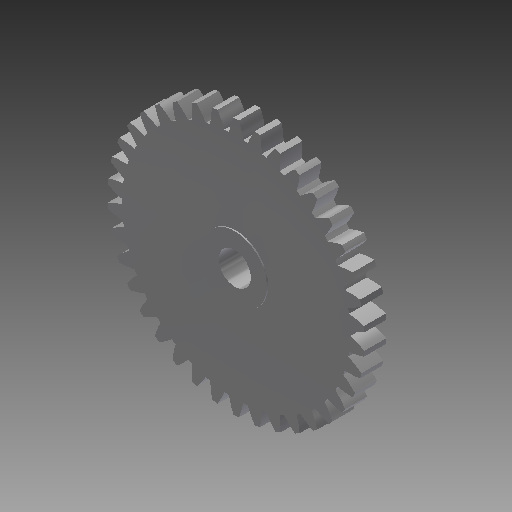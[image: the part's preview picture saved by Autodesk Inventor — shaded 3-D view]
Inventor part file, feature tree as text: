
AUTODESK INVENTOR PART (.ipt)
format: ipt  version: 2017 (Build 210142000, 142)  size: 308,736 bytes
history: native  units: mm (DEFAULTED — no unit token found)
features: sketch x5, extrude x4, plane x3, other x3
ambient origin geometry x8: Origin, YZ Plane, XZ Plane, XY Plane, X Axis, Y Axis, Z Axis, Center Point
bodies: Solid1 (feature_tree)
feature tree (15):
  extrude  "Extrusion1"  Depth=1.7mm TaperAngle=0.0deg
  plane  "Work Plane2"
  plane  "Work Plane8"
  plane  "Work Plane9"
  other  "Spur Gear"
  extrude  "Extrusion2"  Depth=10.0mm TaperAngle=0.0deg
  extrude  "Extrusion3"  Depth=0.826735mm TaperAngle=0.0deg
  extrude  "Extrusion4"  TaperAngle=0.0deg  [1 undecoded]
  sketch  "Sketch1"  dims[d0=20.0mm d1=1.7mm d2=0.0mm]
  sketch  "Sketch2"  dims[d3=19.0mm d4=10.0mm d5=0.0mm]
  other  "Srf1"
  sketch  "Sketch3"  dims[d16=14.5mm d17=0.0mm d34=0.826735mm]
  sketch  "Sketch4"  dims[d39=0.0mm d41=0.0mm]
  sketch  "Sketch5"  dims[d43=14.5mm d46=14.5mm d47=0.0mm d48=0.0mm d49=5.0mm d50=1.5mm d51=0.0mm d52=5.0mm d53=0.1mm d54=0.0mm d55=2.5mm d56=0.1mm d57=0.0mm]
  other  "Pitch Diameter"
note: 1 required parameter value undecoded (feature->parameter linkage not recoverable at this tier; creation-order binding heuristic only, values carry confidence <= 0.55)
